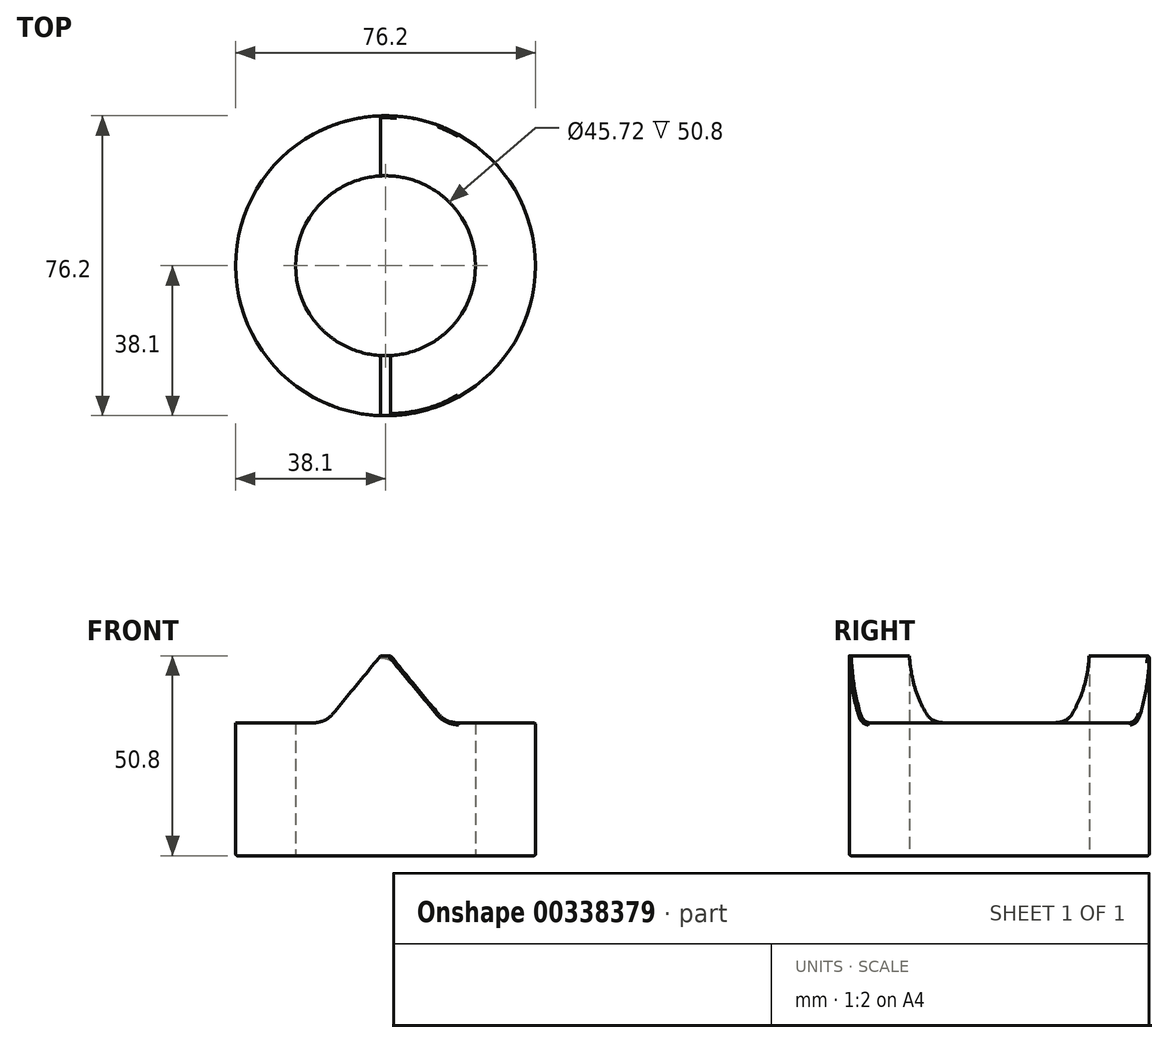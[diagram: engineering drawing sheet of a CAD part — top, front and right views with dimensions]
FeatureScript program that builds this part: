
annotation { "Feature Type Name" : "Feature", "Feature Type Description" : "" }
export const myFeature = defineFeature(function(context is Context, id is Id, definition is map)
    precondition{}
    {
        {
            var Q0;
            Q0=qCreatedBy(makeId("Top.planeOp"),FACE);
            var sketch = newSketch(context, id + "F0", { "sketchPlane" : qUnion([Q0])});
            skCircle(sketch, "E0", {"center": v(0, 0) * mm, "radius": 38.1 * mm});
            skCircle(sketch, "E1", {"center": v(0, 0) * mm, "radius": 22.86 * mm});
            skSolve(sketch);
        }
        {
            var Q0;
            Q0=makeQuery(id+"F0.imprint","IMPRINT",FACE,{"disambiguationData":[TD([[makeQuery(id+"F0.imprint","IMPRINT",EDGE,{"derivedFrom":sQuery(id+"F0.wireOp",EDGE,"E0")}),1.0]])]});
            extrude(context, id + "F1", {"entities" : qUnion([Q0]), "depth" : 50.8 * mm});
        }
        {
            var Q0;
            Q0=qCreatedBy(makeId("Front.planeOp"),FACE);
            cPlane(context, id + "F2", {"entities" : qUnion([Q0]), "cplaneType" : CPlaneType.OFFSET, "offset" : 45.47 * mm, "width" : 152.4 * mm, "height" : 152.4 * mm});
        }
        {
            var Q0;
            Q0=qCreatedBy(id+"F2.planeOp",FACE);
            var sketch = newSketch(context, id + "F3", { "sketchPlane" : qUnion([Q0])});
            skLineSegment(sketch, "E2.top", {"start": v(-38.1, 33.78) * mm, "end": v(-18.24, 33.78) * mm});
            skLineSegment(sketch, "E2.left", {"start": v(-38.1, 0) * mm, "end": v(-38.1, 33.78) * mm});
            skLineSegment(sketch, "E2.right", {"start": v(38.1, 0) * mm, "end": v(38.1, 33.78) * mm});
            skPoint(sketch, "E2.middle", {"position": v(0, 0) * mm});
            skLineSegment(sketch, "E3", {"start": v(-38.1, 0) * mm, "end": v(38.1, 0) * mm});
            skPoint(sketch, "E2.bottom.start.orphan", {"position": v(-38.1, -33.78) * mm});
            skPoint(sketch, "E4.orphan", {"position": v(38.1, -33.78) * mm});
            skLineSegment(sketch, "E5", {"start": v(0, 50.8) * mm, "end": v(0, 0) * mm});
            skLineSegment(sketch, "E6", {"start": v(-1.24, 50.8) * mm, "end": v(1.24, 50.8) * mm});
            skLineSegment(sketch, "E7", {"start": v(1.29, 50.78) * mm, "end": v(13.33, 36.1) * mm});
            skLineSegment(sketch, "E8", {"start": v(-1.29, 50.78) * mm, "end": v(-13.33, 36.1) * mm});
            skPoint(sketch, "E9.newPointA", {"position": v(-15.24, 33.78) * mm});
            skPoint(sketch, "E9.newPointB", {"position": v(38.1, 33.78) * mm});
            skArc(sketch, "E9.filletArc", {"start": v(-18.24, 33.78) * mm, "mid": v(-15.53, 34.4) * mm, "end": v(-13.33, 36.1) * mm});
            skLineSegment(sketch, "E10", {"start": v(38.1, 33.78) * mm, "end": v(18.24, 33.78) * mm});
            skPoint(sketch, "E11.visualSharp", {"position": v(15.24, 33.78) * mm});
            skArc(sketch, "E11.filletArc", {"start": v(13.33, 36.1) * mm, "mid": v(15.53, 34.4) * mm, "end": v(18.24, 33.78) * mm});
            skPoint(sketch, "E12.visualSharp", {"position": v(1.27, 50.8) * mm});
            skPoint(sketch, "E13.visualSharp", {"position": v(-1.27, 50.8) * mm});
            skLineSegment(sketch, "E14", {"start": v(-38.1, 33.78) * mm, "end": v(-38.1, 51.1) * mm});
            skLineSegment(sketch, "E15", {"start": v(38.1, 33.78) * mm, "end": v(38.1, 53.42) * mm});
            skLineSegment(sketch, "E16", {"start": v(-0.13, 50.8) * mm, "end": v(-38.1, 50.8) * mm});
            skLineSegment(sketch, "E17", {"start": v(-38.1, 50.8) * mm, "end": v(38.1, 50.8) * mm});
            skLineSegment(sketch, "E18", {"start": v(-1.29, 50.78) * mm, "end": v(-1.27, 50.8) * mm});
            skLineSegment(sketch, "E19", {"start": v(1.29, 50.78) * mm, "end": v(1.27, 50.8) * mm});
            skSolve(sketch);
        }
        {
            var Q0;
            {var subQ1=sQuery(id+"F3.wireOp",EDGE,"E2.top");Q0=makeQuery(id+"F3.imprint","IMPRINT",FACE,{"disambiguationData":[TD([[makeQuery(id+"F3.imprint","IMPRINT",EDGE,{"derivedFrom":subQ1}),1.0]])]});}
            var Q1;
            Q1=makeQuery(id+"F3.imprint","IMPRINT",FACE,{"disambiguationData":[TD([[makeQuery(id+"F3.imprint","IMPRINT",EDGE,{"derivedFrom":sQuery(id+"F3.wireOp",EDGE,"E7")}),1.0]])]});
            extrude(context, id + "F4", {"entities" : qUnion([Q0, Q1]), "operationType" : NewBodyOperationType.REMOVE, "endBound" : BoundingType.THROUGH_ALL, "oppositeDirection" : true, "depth" : 25.4 * mm});
        }
        {
            var Q0;
            Q0=makeQuery(id+"F4.boolean.opBoolean","COPY",EDGE,{"disambiguationData":[OD(0.0)],"derivedFrom":makeQuery(id+"F4.opExtrude","SWEPT_EDGE",EDGE,{"disambiguationData":[OSD([sQuery(id+"F3.wireOp",EDGE,"E17"),sQuery(id+"F3.wireOp",EDGE,"E19")])]})});
            var Q1;
            Q1=makeQuery(id+"F4.boolean.opBoolean","COPY",EDGE,{"disambiguationData":[OD(0.0)],"derivedFrom":makeQuery(id+"F4.opExtrude","SWEPT_EDGE",EDGE,{"disambiguationData":[OSD([sQuery(id+"F3.wireOp",EDGE,"E17"),sQuery(id+"F3.wireOp",EDGE,"E18")])]})});
            var Q2;
            Q2=makeQuery(id+"F4.boolean.opBoolean","COPY",EDGE,{"disambiguationData":[OD(1.0)],"derivedFrom":makeQuery(id+"F4.opExtrude","SWEPT_EDGE",EDGE,{"disambiguationData":[OSD([sQuery(id+"F3.wireOp",EDGE,"E17"),sQuery(id+"F3.wireOp",EDGE,"E19")])]})});
            var Q3;
            Q3=makeQuery(id+"F4.boolean.opBoolean","COPY",EDGE,{"disambiguationData":[OD(1.0)],"derivedFrom":makeQuery(id+"F4.opExtrude","SWEPT_EDGE",EDGE,{"disambiguationData":[OSD([sQuery(id+"F3.wireOp",EDGE,"E17"),sQuery(id+"F3.wireOp",EDGE,"E18")])]})});
            fillet(context, id + "F5", {"entities" : qUnion([Q0, Q1, Q2, Q3]), "radius" : 5.08 * mm, "tangentPropagation" : true, "allowEdgeOverflow" : false});
        }
        {
            var Q0;
            Q0=makeQuery(id+"F4.boolean.opBoolean","INTERSECT",EDGE,{"derivedFrom":[makeQuery(id+"F1.opExtrude","SWEPT_FACE",FACE,{"disambiguationData":[OSD([sQuery(id+"F0.wireOp",EDGE,"E0")])]}),makeQuery(id+"F4.opExtrude","SWEPT_FACE",FACE,{"disambiguationData":[OSD([sQuery(id+"F3.wireOp",EDGE,"E10")])]})]});
            var Q1;
            Q1=makeQuery(id+"F5.opFillet","BLEND_EDGE",EDGE,{"blendedFrom":[makeQuery(id+"F4.boolean.opBoolean","COPY",EDGE,{"disambiguationData":[OD(0.0)],"derivedFrom":makeQuery(id+"F4.opExtrude","SWEPT_EDGE",EDGE,{"disambiguationData":[OSD([sQuery(id+"F3.wireOp",EDGE,"E17"),sQuery(id+"F3.wireOp",EDGE,"E19")])]})}),makeQuery(id+"F1.opExtrude","SWEPT_FACE",FACE,{"disambiguationData":[OSD([sQuery(id+"F0.wireOp",EDGE,"E0")])]})],"blendedInto":[makeQuery(id+"F1.opExtrude","SWEPT_FACE",FACE,{"disambiguationData":[OSD([sQuery(id+"F0.wireOp",EDGE,"E0")])]})]});
            var Q2;
            Q2=makeQuery(id+"F5.opFillet","BLEND_EDGE",EDGE,{"blendedFrom":[makeQuery(id+"F4.boolean.opBoolean","COPY",EDGE,{"disambiguationData":[OD(0.0)],"derivedFrom":makeQuery(id+"F4.opExtrude","SWEPT_EDGE",EDGE,{"disambiguationData":[OSD([sQuery(id+"F3.wireOp",EDGE,"E17"),sQuery(id+"F3.wireOp",EDGE,"E18")])]})}),makeQuery(id+"F1.opExtrude","SWEPT_FACE",FACE,{"disambiguationData":[OSD([sQuery(id+"F0.wireOp",EDGE,"E0")])]})],"blendedInto":[makeQuery(id+"F1.opExtrude","SWEPT_FACE",FACE,{"disambiguationData":[OSD([sQuery(id+"F0.wireOp",EDGE,"E0")])]})]});
            fillet(context, id + "F6", {"entities" : qUnion([Q0, Q1, Q2]), "radius" : 0.5 * mm, "tangentPropagation" : true, "allowEdgeOverflow" : false});
        }
        {
            var Q0;
            Q0=makeQuery(id+"F1.opExtrude","CAP_EDGE",EDGE,{"disambiguationData":[OSD([sQuery(id+"F0.wireOp",EDGE,"E0")])],"isStart":true});
            fillet(context, id + "F7", {"entities" : qUnion([Q0]), "radius" : 0.5 * mm, "tangentPropagation" : true, "allowEdgeOverflow" : false});
        }
    });
